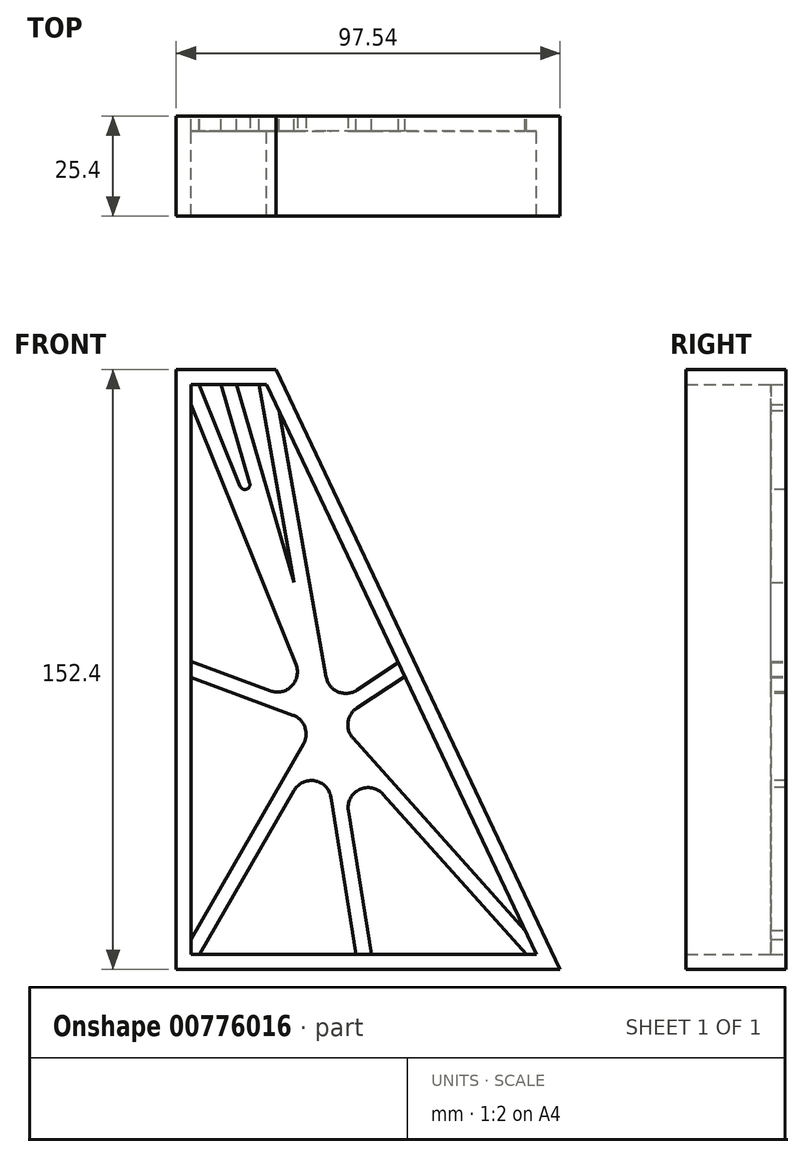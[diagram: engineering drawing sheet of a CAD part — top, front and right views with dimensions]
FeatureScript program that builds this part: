
annotation { "Feature Type Name" : "Feature", "Feature Type Description" : "" }
export const myFeature = defineFeature(function(context is Context, id is Id, definition is map)
    precondition{}
    {
        {
            var Q0;
            Q0=qCreatedBy(makeId("Front.planeOp"),FACE);
            var sketch = newSketch(context, id + "F0", { "sketchPlane" : qUnion([Q0])});
            skLineSegment(sketch, "E0", {"start": v(0, 0) * mm, "end": v(97.54, 0) * mm});
            skLineSegment(sketch, "E1", {"start": v(97.54, 0) * mm, "end": v(25.4, 152.4) * mm});
            skLineSegment(sketch, "E2", {"start": v(25.4, 152.4) * mm, "end": v(0, 152.4) * mm});
            skLineSegment(sketch, "E3", {"start": v(0, 152.4) * mm, "end": v(0, 0) * mm});
            skLineSegment(sketch, "E4", {"start": v(3.8, 148.6) * mm, "end": v(3.81, 3.8) * mm});
            skLineSegment(sketch, "E5", {"start": v(3.81, 3.8) * mm, "end": v(91.52, 3.81) * mm});
            skLineSegment(sketch, "E6", {"start": v(91.52, 3.8) * mm, "end": v(22.99, 148.6) * mm});
            skLineSegment(sketch, "E7", {"start": v(22.99, 148.6) * mm, "end": v(3.8, 148.6) * mm});
            skSolve(sketch);
        }
        {
            var Q0;
            Q0=makeQuery(id+"F0.imprint","IMPRINT",FACE,{"disambiguationData":[TD([[makeQuery(id+"F0.imprint","IMPRINT",EDGE,{"derivedFrom":sQuery(id+"F0.wireOp",EDGE,"E0")}),1.0]])]});
            extrude(context, id + "F1", {"entities" : qUnion([Q0]), "depth" : 25.4 * mm, "offsetDistance" : 25.4 * mm});
        }
        {
            var Q0;
            Q0=makeQuery(id+"F1.opExtrude","CAP_FACE",FACE,{"disambiguationData":[OSD([sQuery(id+"F0.wireOp",EDGE,"E0"),sQuery(id+"F0.wireOp",EDGE,"E1"),sQuery(id+"F0.wireOp",EDGE,"E2"),sQuery(id+"F0.wireOp",EDGE,"E3"),sQuery(id+"F0.wireOp",EDGE,"E4"),sQuery(id+"F0.wireOp",EDGE,"E5"),sQuery(id+"F0.wireOp",EDGE,"E6"),sQuery(id+"F0.wireOp",EDGE,"E7")])],"isStart":true});
            var sketch = newSketch(context, id + "F2", { "sketchPlane" : qUnion([Q0])});
            skPoint(sketch, "E8", {"position": v(-57.25, 76.2) * mm});
            skPoint(sketch, "E9", {"position": v(-3.8, 76.2) * mm});
            skPoint(sketch, "E10", {"position": v(-13.4, 148.6) * mm});
            skPoint(sketch, "E11", {"position": v(-47.66, 3.81) * mm});
            skLineSegment(sketch, "E12", {"start": v(-91.52, 3.8) * mm, "end": v(-38.1, 63.5) * mm, "construction": true});
            skLineSegment(sketch, "E13", {"start": v(-38.1, 63.5) * mm, "end": v(-47.66, 3.81) * mm, "construction": true});
            skLineSegment(sketch, "E14", {"start": v(-3.8, 3.8) * mm, "end": v(-38.1, 63.5) * mm, "construction": true});
            skLineSegment(sketch, "E15", {"start": v(-57.25, 76.2) * mm, "end": v(-38.1, 63.5) * mm, "construction": true});
            skLineSegment(sketch, "E16", {"start": v(-3.8, 76.2) * mm, "end": v(-38.1, 63.5) * mm, "construction": true});
            skLineSegment(sketch, "E17", {"start": v(-22.99, 148.6) * mm, "end": v(-38.1, 63.5) * mm, "construction": true});
            skLineSegment(sketch, "E18", {"start": v(-13.4, 148.6) * mm, "end": v(-38.1, 63.5) * mm, "construction": true});
            skLineSegment(sketch, "E19", {"start": v(-3.8, 148.6) * mm, "end": v(-38.1, 63.5) * mm, "construction": true});
            skLineSegment(sketch, "E20", {"start": v(-56.43, 77.94) * mm, "end": v(-39.47, 66.7) * mm});
            skLineSegment(sketch, "E21", {"start": v(-39.47, 66.7) * mm, "end": v(-26.08, 142.05) * mm});
            skLineSegment(sketch, "E22", {"start": v(-58.08, 74.46) * mm, "end": v(-40.99, 63.13) * mm});
            skLineSegment(sketch, "E23", {"start": v(-40.99, 63.13) * mm, "end": v(-88.65, 9.87) * mm});
            skLineSegment(sketch, "E24", {"start": v(-88.96, 3.81) * mm, "end": v(-41, 57.4) * mm});
            skLineSegment(sketch, "E25", {"start": v(-41, 57.4) * mm, "end": v(-49.6, 3.81) * mm});
            skLineSegment(sketch, "E26", {"start": v(-45.73, 3.8) * mm, "end": v(-37.07, 57.88) * mm});
            skLineSegment(sketch, "E27", {"start": v(-37.07, 57.88) * mm, "end": v(-6, 3.8) * mm});
            skLineSegment(sketch, "E28", {"start": v(-3.81, 7.63) * mm, "end": v(-35.33, 62.5) * mm});
            skLineSegment(sketch, "E29", {"start": v(-35.33, 62.5) * mm, "end": v(-3.81, 74.17) * mm});
            skLineSegment(sketch, "E30", {"start": v(-3.8, 78.23) * mm, "end": v(-34.72, 66.78) * mm});
            skLineSegment(sketch, "E31", {"start": v(-34.72, 66.78) * mm, "end": v(-3.8, 143.5) * mm});
            skLineSegment(sketch, "E32", {"start": v(-5.86, 148.6) * mm, "end": v(-25.72, 99.33) * mm});
            skLineSegment(sketch, "E33", {"start": v(-25.72, 99.33) * mm, "end": v(-11.42, 148.6) * mm});
            skLineSegment(sketch, "E34", {"start": v(-15.38, 148.6) * mm, "end": v(-29.99, 98.27) * mm});
            skLineSegment(sketch, "E35", {"start": v(-29.99, 98.27) * mm, "end": v(-21.05, 148.6) * mm});
            skLineSegment(sketch, "E36", {"start": v(-26.08, 142.05) * mm, "end": v(-22.99, 148.6) * mm});
            skLineSegment(sketch, "E37", {"start": v(-21.05, 148.6) * mm, "end": v(-22.99, 148.6) * mm});
            skLineSegment(sketch, "E38", {"start": v(-15.38, 148.6) * mm, "end": v(-11.42, 148.6) * mm});
            skLineSegment(sketch, "E39", {"start": v(-5.86, 148.6) * mm, "end": v(-3.8, 148.6) * mm});
            skLineSegment(sketch, "E40", {"start": v(-3.8, 143.5) * mm, "end": v(-3.8, 148.6) * mm});
            skLineSegment(sketch, "E41", {"start": v(-3.81, 74.17) * mm, "end": v(-3.8, 78.23) * mm});
            skLineSegment(sketch, "E42", {"start": v(-58.08, 74.46) * mm, "end": v(-56.43, 77.94) * mm});
            skLineSegment(sketch, "E43", {"start": v(-88.96, 3.81) * mm, "end": v(-91.52, 3.81) * mm});
            skLineSegment(sketch, "E44", {"start": v(-88.65, 9.87) * mm, "end": v(-91.52, 3.8) * mm});
            skLineSegment(sketch, "E45", {"start": v(-49.6, 3.81) * mm, "end": v(-45.73, 3.8) * mm});
            skLineSegment(sketch, "E46", {"start": v(-6, 3.8) * mm, "end": v(-3.81, 3.8) * mm});
            skLineSegment(sketch, "E47", {"start": v(-3.81, 3.8) * mm, "end": v(-3.81, 7.63) * mm});
            skSolve(sketch);
        }
        {
            var Q0;
            Q0=makeQuery(id+"F2.imprint","IMPRINT",FACE,{"disambiguationData":[TD([[makeQuery(id+"F2.imprint","IMPRINT",EDGE,{"derivedFrom":sQuery(id+"F2.wireOp",EDGE,"E20")}),-1.0]])]});
            extrude(context, id + "F3", {"entities" : qUnion([Q0]), "operationType" : NewBodyOperationType.ADD, "oppositeDirection" : true, "depth" : 3.8 * mm, "offsetDistance" : 25.4 * mm});
        }
        {
            var Q0;
            Q0=makeQuery(id+"F3.opExtrude","SWEPT_EDGE",EDGE,{"disambiguationData":[OSD([sQuery(id+"F2.wireOp",EDGE,"E22"),sQuery(id+"F2.wireOp",EDGE,"E23")])]});
            var Q1;
            Q1=makeQuery(id+"F3.opExtrude","SWEPT_EDGE",EDGE,{"disambiguationData":[OSD([sQuery(id+"F2.wireOp",EDGE,"E24"),sQuery(id+"F2.wireOp",EDGE,"E25")])]});
            var Q2;
            Q2=makeQuery(id+"F3.opExtrude","SWEPT_EDGE",EDGE,{"disambiguationData":[OSD([sQuery(id+"F2.wireOp",EDGE,"E28"),sQuery(id+"F2.wireOp",EDGE,"E29")])]});
            var Q3;
            Q3=makeQuery(id+"F3.opExtrude","SWEPT_EDGE",EDGE,{"disambiguationData":[OSD([sQuery(id+"F2.wireOp",EDGE,"E26"),sQuery(id+"F2.wireOp",EDGE,"E27")])]});
            var Q4;
            Q4=makeQuery(id+"F3.opExtrude","SWEPT_EDGE",EDGE,{"disambiguationData":[OSD([sQuery(id+"F2.wireOp",EDGE,"E20"),sQuery(id+"F2.wireOp",EDGE,"E21")])]});
            var Q5;
            Q5=makeQuery(id+"F3.opExtrude","SWEPT_EDGE",EDGE,{"disambiguationData":[OSD([sQuery(id+"F2.wireOp",EDGE,"E30"),sQuery(id+"F2.wireOp",EDGE,"E31")])]});
            fillet(context, id + "F4", {"entities" : qUnion([Q0, Q1, Q2, Q3, Q4, Q5]), "radius" : 5.08 * mm, "tangentPropagation" : true, "allowEdgeOverflow" : false});
        }
        {
            var Q0;
            Q0=makeQuery(id+"F3.opExtrude","SWEPT_EDGE",EDGE,{"disambiguationData":[OSD([sQuery(id+"F2.wireOp",EDGE,"E32"),sQuery(id+"F2.wireOp",EDGE,"E33")])]});
            fillet(context, id + "F5", {"entities" : qUnion([Q0]), "radius" : 1.27 * mm, "tangentPropagation" : true, "allowEdgeOverflow" : false});
        }
    });
